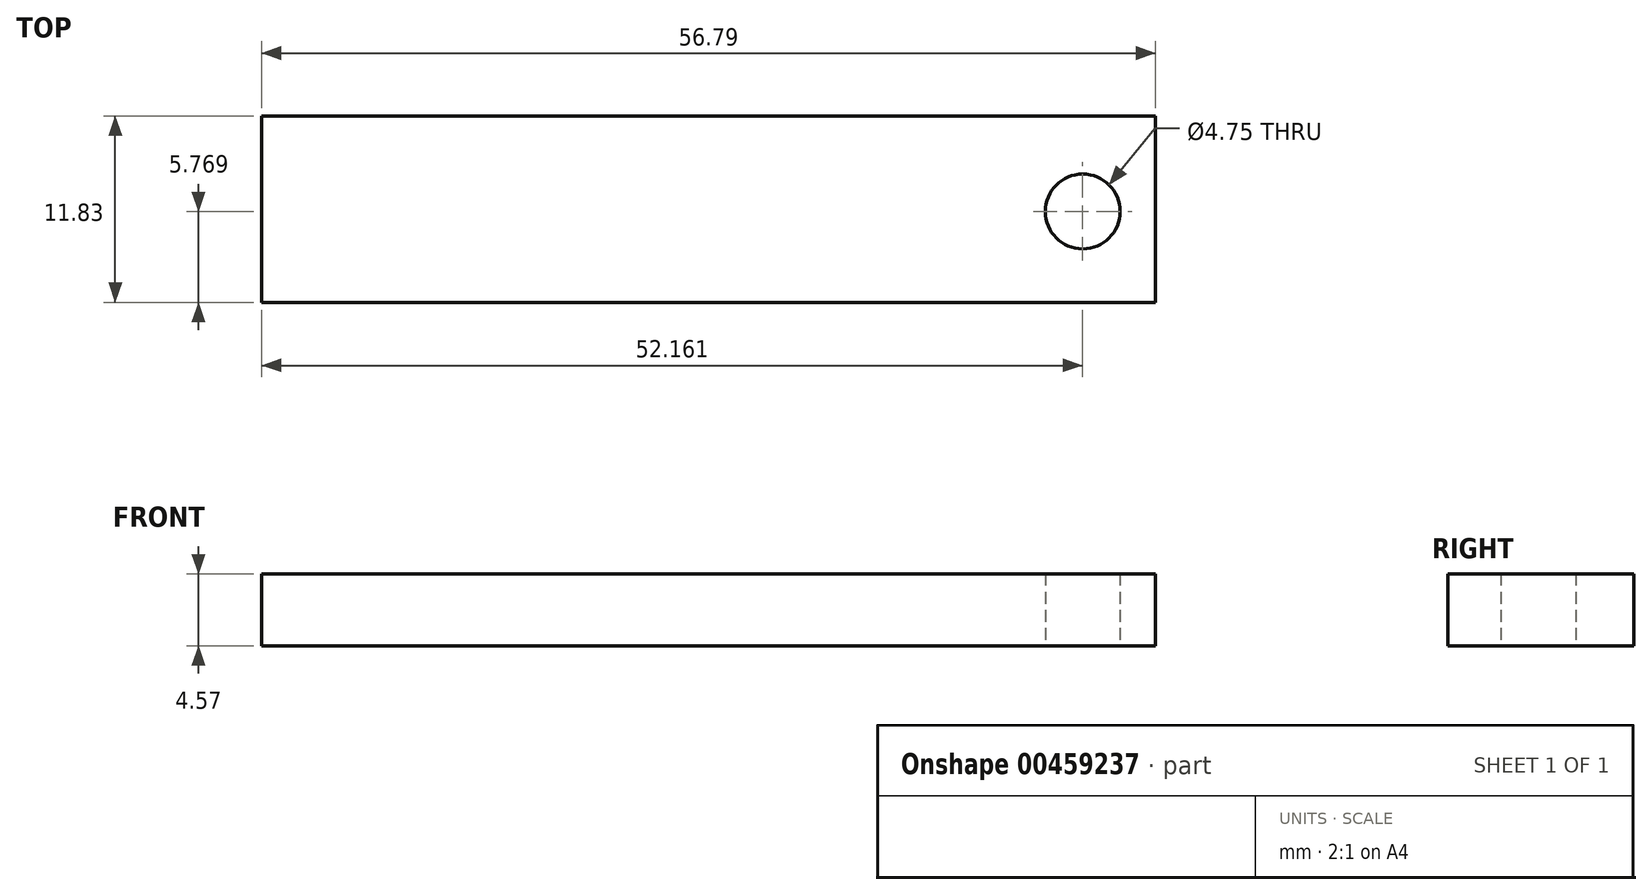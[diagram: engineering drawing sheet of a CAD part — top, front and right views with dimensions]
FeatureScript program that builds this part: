
annotation { "Feature Type Name" : "Feature", "Feature Type Description" : "" }
export const myFeature = defineFeature(function(context is Context, id is Id, definition is map)
    precondition{}
    {
        {
            var Q0;
            Q0=qCreatedBy(makeId("Top.planeOp"),FACE);
            var sketch = newSketch(context, id + "F0", { "sketchPlane" : qUnion([Q0])});
            skLineSegment(sketch, "E0.bottom", {"start": v(0, 0) * mm, "end": v(56.8, 0) * mm});
            skLineSegment(sketch, "E0.top", {"start": v(0, 11.83) * mm, "end": v(56.8, 11.83) * mm});
            skLineSegment(sketch, "E0.left", {"start": v(0, 0) * mm, "end": v(0, 11.83) * mm});
            skLineSegment(sketch, "E0.right", {"start": v(56.8, 0) * mm, "end": v(56.8, 11.83) * mm});
            skCircle(sketch, "E1", {"center": v(52.16, 5.77) * mm, "radius": 2.38 * mm});
            skSolve(sketch);
        }
        {
            var Q0;
            Q0 = qSketchRegion(id + "F0", true);
            extrude(context, id + "F1", {"entities" : qUnion([Q0]), "depth" : 4.57 * mm});
        }
    });
